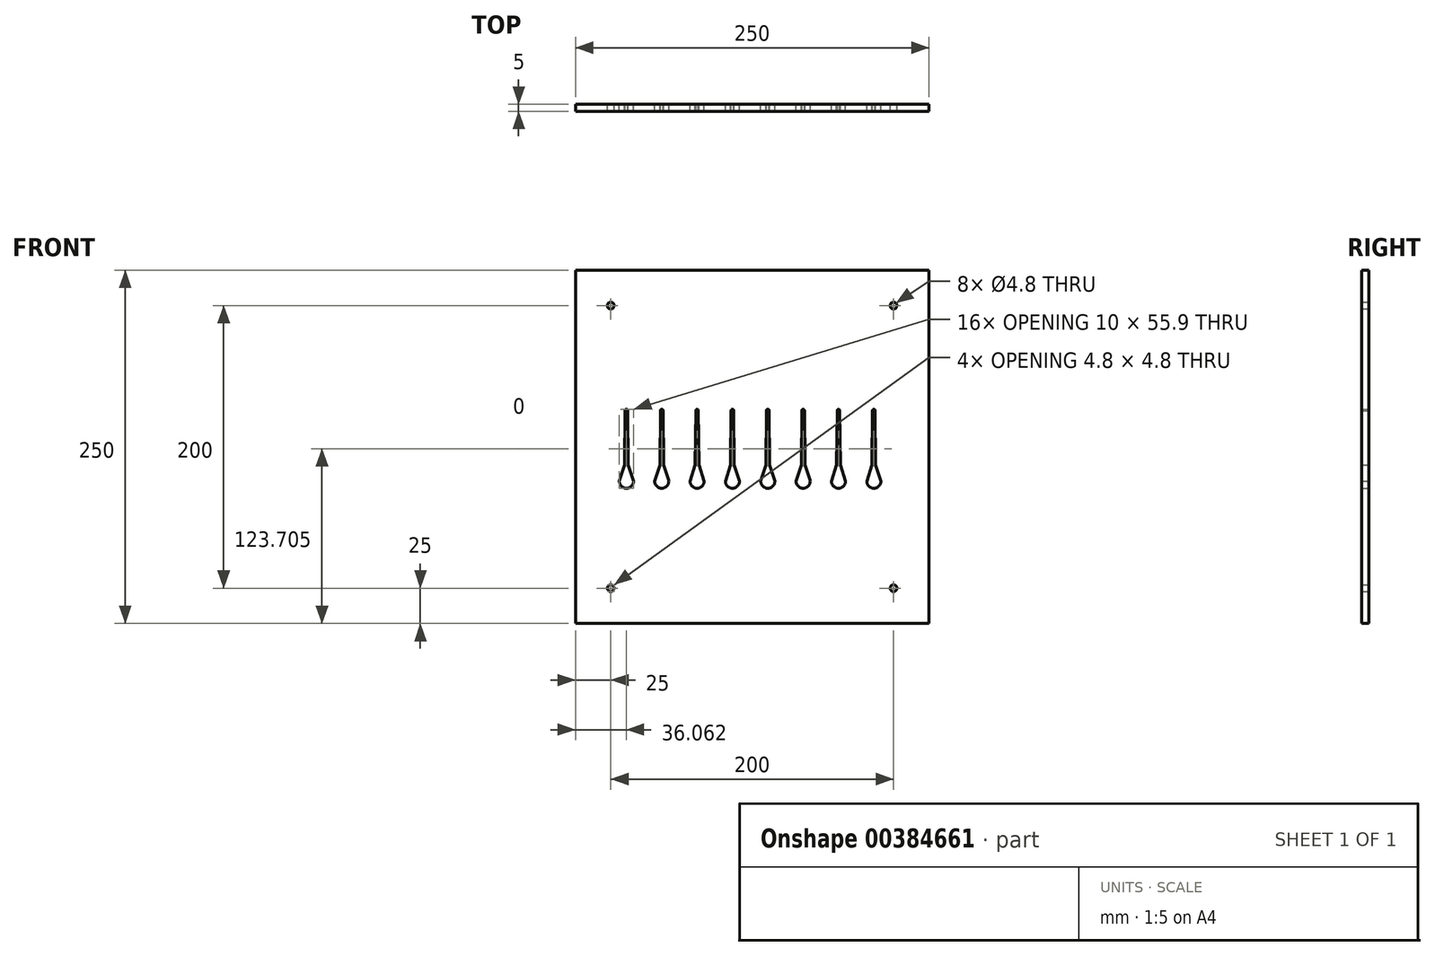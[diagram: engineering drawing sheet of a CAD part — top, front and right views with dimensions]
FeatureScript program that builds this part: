
annotation { "Feature Type Name" : "Feature", "Feature Type Description" : "" }
export const myFeature = defineFeature(function(context is Context, id is Id, definition is map)
    precondition{}
    {
        {
            var Q0;
            Q0=qCreatedBy(makeId("Front.planeOp"),FACE);
            var sketch = newSketch(context, id + "F0", { "sketchPlane" : qUnion([Q0])});
            skLineSegment(sketch, "E0.bottom", {"start": v(0, 0) * mm, "end": v(250, 0) * mm});
            skLineSegment(sketch, "E0.top", {"start": v(0, -250) * mm, "end": v(250, -250) * mm});
            skLineSegment(sketch, "E0.left", {"start": v(0, 0) * mm, "end": v(0, -250) * mm});
            skLineSegment(sketch, "E0.right", {"start": v(250, 0) * mm, "end": v(250, -250) * mm});
            skArc(sketch, "E1", {"start": v(31.06, -149.24) * mm, "mid": v(36.06, -154.24) * mm, "end": v(41.06, -149.24) * mm});
            skLineSegment(sketch, "E2", {"start": v(0, -99.24) * mm, "end": v(250, -99.24) * mm, "construction": true});
            skLineSegment(sketch, "E3", {"start": v(36.06, -149.24) * mm, "end": v(36.06, -99.24) * mm, "construction": true});
            skArc(sketch, "E4", {"start": v(36.96, -99.24) * mm, "mid": v(36.06, -98.34) * mm, "end": v(35.16, -99.24) * mm});
            skPoint(sketch, "E5", {"position": v(25, -25) * mm});
            skLineSegment(sketch, "E6", {"start": v(125, 0) * mm, "end": v(125, -250) * mm, "construction": true});
            skLineSegment(sketch, "E7", {"start": v(250, -125) * mm, "end": v(0, -125) * mm, "construction": true});
            skPoint(sketch, "E8.MirrorP", {"position": v(225, -25) * mm});
            skPoint(sketch, "E9.MirrorP", {"position": v(225, -225) * mm});
            skPoint(sketch, "E10.MirrorP", {"position": v(25, -225) * mm});
            skLineSegment(sketch, "E11", {"start": v(26.42, -137.87) * mm, "end": v(47.77, -137.87) * mm, "construction": true});
            skLineSegment(sketch, "E12", {"start": v(31.06, -149.24) * mm, "end": v(34.76, -137.87) * mm});
            skLineSegment(sketch, "E13", {"start": v(34.76, -137.87) * mm, "end": v(35.16, -99.24) * mm});
            skLineSegment(sketch, "E14.MirrorCS", {"start": v(37.36, -137.87) * mm, "end": v(36.96, -99.24) * mm});
            skLineSegment(sketch, "E15.MirrorCS", {"start": v(41.06, -149.24) * mm, "end": v(37.36, -137.87) * mm});
            skLineSegment(sketch, "E16.1.0.0", {"start": v(66.06, -149.24) * mm, "end": v(62.36, -137.87) * mm});
            skLineSegment(sketch, "E16.1.0.1", {"start": v(62.36, -137.87) * mm, "end": v(61.96, -99.24) * mm});
            skLineSegment(sketch, "E16.1.0.2", {"start": v(51.42, -137.87) * mm, "end": v(72.77, -137.87) * mm, "construction": true});
            skLineSegment(sketch, "E16.1.0.3", {"start": v(61.06, -149.24) * mm, "end": v(61.06, -99.24) * mm, "construction": true});
            skArc(sketch, "E16.1.0.4", {"start": v(56.06, -149.24) * mm, "mid": v(61.06, -154.24) * mm, "end": v(66.06, -149.24) * mm});
            skLineSegment(sketch, "E16.1.0.5", {"start": v(59.76, -137.87) * mm, "end": v(60.16, -99.24) * mm});
            skLineSegment(sketch, "E16.1.0.6", {"start": v(56.06, -149.24) * mm, "end": v(59.76, -137.87) * mm});
            skArc(sketch, "E16.1.0.7", {"start": v(61.96, -99.24) * mm, "mid": v(61.06, -98.34) * mm, "end": v(60.16, -99.24) * mm});
            skLineSegment(sketch, "E16.2.0.0", {"start": v(91.06, -149.24) * mm, "end": v(87.36, -137.87) * mm});
            skLineSegment(sketch, "E16.2.0.1", {"start": v(87.36, -137.87) * mm, "end": v(86.96, -99.24) * mm});
            skLineSegment(sketch, "E16.2.0.2", {"start": v(76.42, -137.87) * mm, "end": v(97.77, -137.87) * mm, "construction": true});
            skLineSegment(sketch, "E16.2.0.3", {"start": v(86.06, -149.24) * mm, "end": v(86.06, -99.24) * mm, "construction": true});
            skArc(sketch, "E16.2.0.4", {"start": v(81.06, -149.24) * mm, "mid": v(86.06, -154.24) * mm, "end": v(91.06, -149.24) * mm});
            skLineSegment(sketch, "E16.2.0.5", {"start": v(84.76, -137.87) * mm, "end": v(85.16, -99.24) * mm});
            skLineSegment(sketch, "E16.2.0.6", {"start": v(81.06, -149.24) * mm, "end": v(84.76, -137.87) * mm});
            skArc(sketch, "E16.2.0.7", {"start": v(86.96, -99.24) * mm, "mid": v(86.06, -98.34) * mm, "end": v(85.16, -99.24) * mm});
            skLineSegment(sketch, "E16.3.0.0", {"start": v(116.06, -149.24) * mm, "end": v(112.36, -137.87) * mm});
            skLineSegment(sketch, "E16.3.0.1", {"start": v(112.36, -137.87) * mm, "end": v(111.96, -99.24) * mm});
            skLineSegment(sketch, "E16.3.0.2", {"start": v(101.42, -137.87) * mm, "end": v(122.77, -137.87) * mm, "construction": true});
            skLineSegment(sketch, "E16.3.0.3", {"start": v(111.06, -149.24) * mm, "end": v(111.06, -99.24) * mm, "construction": true});
            skArc(sketch, "E16.3.0.4", {"start": v(106.06, -149.24) * mm, "mid": v(111.06, -154.24) * mm, "end": v(116.06, -149.24) * mm});
            skLineSegment(sketch, "E16.3.0.5", {"start": v(109.76, -137.87) * mm, "end": v(110.16, -99.24) * mm});
            skLineSegment(sketch, "E16.3.0.6", {"start": v(106.06, -149.24) * mm, "end": v(109.76, -137.87) * mm});
            skArc(sketch, "E16.3.0.7", {"start": v(111.96, -99.24) * mm, "mid": v(111.06, -98.34) * mm, "end": v(110.16, -99.24) * mm});
            skLineSegment(sketch, "E16.4.0.0", {"start": v(141.06, -149.24) * mm, "end": v(137.36, -137.87) * mm});
            skLineSegment(sketch, "E16.4.0.1", {"start": v(137.36, -137.87) * mm, "end": v(136.96, -99.24) * mm});
            skLineSegment(sketch, "E16.4.0.2", {"start": v(126.42, -137.87) * mm, "end": v(147.77, -137.87) * mm, "construction": true});
            skLineSegment(sketch, "E16.4.0.3", {"start": v(136.06, -149.24) * mm, "end": v(136.06, -99.24) * mm, "construction": true});
            skArc(sketch, "E16.4.0.4", {"start": v(131.06, -149.24) * mm, "mid": v(136.06, -154.24) * mm, "end": v(141.06, -149.24) * mm});
            skLineSegment(sketch, "E16.4.0.5", {"start": v(134.76, -137.87) * mm, "end": v(135.16, -99.24) * mm});
            skLineSegment(sketch, "E16.4.0.6", {"start": v(131.06, -149.24) * mm, "end": v(134.76, -137.87) * mm});
            skArc(sketch, "E16.4.0.7", {"start": v(136.96, -99.24) * mm, "mid": v(136.06, -98.34) * mm, "end": v(135.16, -99.24) * mm});
            skLineSegment(sketch, "E16.5.0.0", {"start": v(166.06, -149.24) * mm, "end": v(162.36, -137.87) * mm});
            skLineSegment(sketch, "E16.5.0.1", {"start": v(162.36, -137.87) * mm, "end": v(161.96, -99.24) * mm});
            skLineSegment(sketch, "E16.5.0.2", {"start": v(151.42, -137.87) * mm, "end": v(172.77, -137.87) * mm, "construction": true});
            skLineSegment(sketch, "E16.5.0.3", {"start": v(161.06, -149.24) * mm, "end": v(161.06, -99.24) * mm, "construction": true});
            skArc(sketch, "E16.5.0.4", {"start": v(156.06, -149.24) * mm, "mid": v(161.06, -154.24) * mm, "end": v(166.06, -149.24) * mm});
            skLineSegment(sketch, "E16.5.0.5", {"start": v(159.76, -137.87) * mm, "end": v(160.16, -99.24) * mm});
            skLineSegment(sketch, "E16.5.0.6", {"start": v(156.06, -149.24) * mm, "end": v(159.76, -137.87) * mm});
            skArc(sketch, "E16.5.0.7", {"start": v(161.96, -99.24) * mm, "mid": v(161.06, -98.34) * mm, "end": v(160.16, -99.24) * mm});
            skLineSegment(sketch, "E16.6.0.0", {"start": v(191.06, -149.24) * mm, "end": v(187.36, -137.87) * mm});
            skLineSegment(sketch, "E16.6.0.1", {"start": v(187.36, -137.87) * mm, "end": v(186.96, -99.24) * mm});
            skLineSegment(sketch, "E16.6.0.2", {"start": v(176.42, -137.87) * mm, "end": v(197.77, -137.87) * mm, "construction": true});
            skLineSegment(sketch, "E16.6.0.3", {"start": v(186.06, -149.24) * mm, "end": v(186.06, -99.24) * mm, "construction": true});
            skArc(sketch, "E16.6.0.4", {"start": v(181.06, -149.24) * mm, "mid": v(186.06, -154.24) * mm, "end": v(191.06, -149.24) * mm});
            skLineSegment(sketch, "E16.6.0.5", {"start": v(184.76, -137.87) * mm, "end": v(185.16, -99.24) * mm});
            skLineSegment(sketch, "E16.6.0.6", {"start": v(181.06, -149.24) * mm, "end": v(184.76, -137.87) * mm});
            skArc(sketch, "E16.6.0.7", {"start": v(186.96, -99.24) * mm, "mid": v(186.06, -98.34) * mm, "end": v(185.16, -99.24) * mm});
            skLineSegment(sketch, "E16.7.0.0", {"start": v(216.06, -149.24) * mm, "end": v(212.36, -137.87) * mm});
            skLineSegment(sketch, "E16.7.0.1", {"start": v(212.36, -137.87) * mm, "end": v(211.96, -99.24) * mm});
            skLineSegment(sketch, "E16.7.0.2", {"start": v(201.42, -137.87) * mm, "end": v(222.77, -137.87) * mm, "construction": true});
            skLineSegment(sketch, "E16.7.0.3", {"start": v(211.06, -149.24) * mm, "end": v(211.06, -99.24) * mm, "construction": true});
            skArc(sketch, "E16.7.0.4", {"start": v(206.06, -149.24) * mm, "mid": v(211.06, -154.24) * mm, "end": v(216.06, -149.24) * mm});
            skLineSegment(sketch, "E16.7.0.5", {"start": v(209.76, -137.87) * mm, "end": v(210.16, -99.24) * mm});
            skLineSegment(sketch, "E16.7.0.6", {"start": v(206.06, -149.24) * mm, "end": v(209.76, -137.87) * mm});
            skArc(sketch, "E16.7.0.7", {"start": v(211.96, -99.24) * mm, "mid": v(211.06, -98.34) * mm, "end": v(210.16, -99.24) * mm});
            skLineSegment(sketch, "E16.direction1", {"start": v(31.06, -149.24) * mm, "end": v(56.06, -149.24) * mm, "construction": true});
            skSolve(sketch);
        }
        {
            var Q0;
            Q0 = qSketchRegion(id + "F0", true);
            extrude(context, id + "F1", {"entities" : qUnion([Q0]), "depth" : 5 * mm});
        }
        {
            var Q0;
            Q0=sQuery(id+"F0.wireOp",VERTEX,"E5");
            var Q1;
            Q1=sQuery(id+"F0.wireOp",VERTEX,"E8.MirrorP");
            var Q2;
            Q2=sQuery(id+"F0.wireOp",VERTEX,"E9.MirrorP");
            var Q3;
            Q3=sQuery(id+"F0.wireOp",VERTEX,"E10.MirrorP");
            var Q4;
            Q4=makeQuery(id+"F1.opExtrude","SWEPT_BODY",BODY,{"disambiguationData":[OSD([sQuery(id+"F0.wireOp",EDGE,"E0.bottom"),sQuery(id+"F0.wireOp",EDGE,"E0.top"),sQuery(id+"F0.wireOp",EDGE,"E0.left"),sQuery(id+"F0.wireOp",EDGE,"E0.right"),sQuery(id+"F0.wireOp",EDGE,"E1"),sQuery(id+"F0.wireOp",EDGE,"E4"),sQuery(id+"F0.wireOp",EDGE,"99dfce45-29b2-44a2-aebb-3510af8edc45"),sQuery(id+"F0.wireOp",EDGE,"c3400214-7838-48be-b747-518353956c410.MirrorCS")])]});
            hole(context, id + "F2", {"style" : HoleStyle.SIMPLE, "endStyle" : HoleEndStyle.THROUGH, "oppositeDirection" : true, "holeDiameter" : 4.8 * mm, "isTappedThrough" : true, "tappedDepth" : 12 * mm, "tapClearance" : 3, "locations" : qUnion([Q0, Q1, Q2, Q3]), "scope" : qUnion([Q4])});
        }
    });
